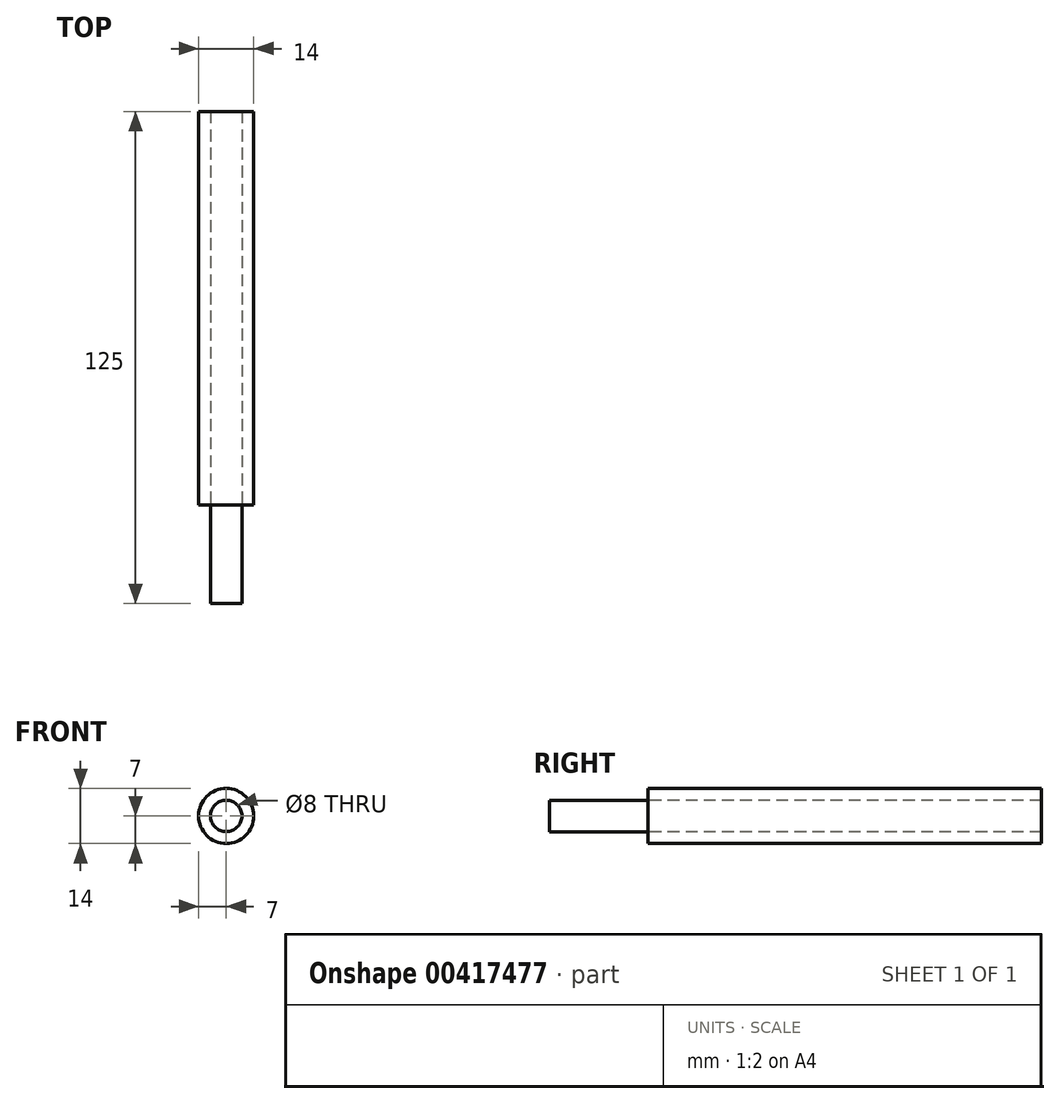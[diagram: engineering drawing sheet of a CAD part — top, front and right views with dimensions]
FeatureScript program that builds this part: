
annotation { "Feature Type Name" : "Feature", "Feature Type Description" : "" }
export const myFeature = defineFeature(function(context is Context, id is Id, definition is map)
    precondition{}
    {
        {
            var Q0;
            Q0=qCreatedBy(makeId("Front.planeOp"),FACE);
            var sketch = newSketch(context, id + "F0", { "sketchPlane" : qUnion([Q0])});
            skLineSegment(sketch, "E0", {"start": v(-72.4, 46.62) * mm, "end": v(-5, 46.62) * mm});
            skLineSegment(sketch, "E1", {"start": v(-5, 46.62) * mm, "end": v(-5, 37.32) * mm});
            skLineSegment(sketch, "E2", {"start": v(-5, 37.32) * mm, "end": v(-22.5, 37.32) * mm});
            skLineSegment(sketch, "E3", {"start": v(-22.5, 37.32) * mm, "end": v(-22.5, -32.68) * mm});
            skLineSegment(sketch, "E4", {"start": v(-22.5, -32.68) * mm, "end": v(-10.25, -43.41) * mm});
            skLineSegment(sketch, "E5", {"start": v(-10.25, -43.41) * mm, "end": v(-78.08, -43.41) * mm});
            skLineSegment(sketch, "E6", {"start": v(-22.5, 33.72) * mm, "end": v(-22.5, 37.32) * mm, "construction": true});
            skCircle(sketch, "E7", {"center": v(0, 0) * mm, "radius": 7 * mm});
            skLineSegment(sketch, "E8", {"start": v(0, 0) * mm, "end": v(0, 0) * mm});
            skLineSegment(sketch, "E9", {"start": v(0, 0) * mm, "end": v(7, 0) * mm, "construction": true});
            skLineSegment(sketch, "E10", {"start": v(-2.29, 6.62) * mm, "end": v(-22.5, 6.62) * mm, "construction": true});
            skCircle(sketch, "E11", {"center": v(0, 0) * mm, "radius": 4 * mm});
            skCircle(sketch, "E12", {"center": v(0, 0) * mm, "radius": 11 * mm});
            skCircle(sketch, "E13", {"center": v(0, 0) * mm, "radius": 9 * mm});
            skSolve(sketch);
        }
        {
            var Q0;
            Q0=sQuery(id+"F0.wireOp",EDGE,"E0");
            var Q1;
            Q1=sQuery(id+"F0.wireOp",EDGE,"E1");
            var Q2;
            Q2=sQuery(id+"F0.wireOp",EDGE,"E2");
            var Q3;
            Q3=sQuery(id+"F0.wireOp",EDGE,"E3");
            var Q4;
            Q4=sQuery(id+"F0.wireOp",EDGE,"E4");
            var Q5;
            Q5=sQuery(id+"F0.wireOp",EDGE,"E5");
            extrude(context, id + "F1", {"bodyType" : ToolBodyType.SURFACE, "surfaceEntities" : qUnion([Q0, Q1, Q2, Q3, Q4, Q5]), "depth" : 150 * mm, "hasSecondDirection" : true, "secondDirectionOppositeDirection" : true, "secondDirectionDepth" : 100 * mm});
        }
        {
            var Q0;
            Q0=makeQuery(id+"F0.imprint","IMPRINT",FACE,{"disambiguationData":[TD([[makeQuery(id+"F0.imprint","IMPRINT",EDGE,{"derivedFrom":sQuery(id+"F0.wireOp",EDGE,"E7")}),1.0]])]});
            extrude(context, id + "F2", {"entities" : qUnion([Q0]), "oppositeDirection" : true, "depth" : 100 * mm, "hasSecondDirection" : true, "secondDirectionOppositeDirection" : false, "secondDirectionDepth" : 0 * mm});
        }
        {
            var Q0;
            Q0=makeQuery(id+"F0.imprint","IMPRINT",FACE,{"disambiguationData":[TD([[makeQuery(id+"F0.imprint","IMPRINT",EDGE,{"derivedFrom":sQuery(id+"F0.wireOp",EDGE,"E11")}),1.0]])]});
            extrude(context, id + "F3", {"entities" : qUnion([Q0]), "depth" : 25 * mm});
        }
    });
